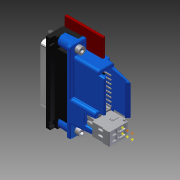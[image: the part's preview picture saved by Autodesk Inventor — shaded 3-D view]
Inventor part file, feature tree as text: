
AUTODESK INVENTOR PART (.ipt)
format: ipt  version: 2011 (Build 150239000, 239)  size: 2,223,616 bytes
history: native  units: in
note: dims shown in document units (in); Inventor stores cm internally (conversion verified against a paired STEP export)
features: other x22, plane x4, pattern_linear x1
ambient origin geometry x8: Origin, YZ Plane, XZ Plane, XY Plane, X Axis, Y Axis, Z Axis, Center Point
bodies: Solid1 (feature_tree)
feature tree (27):
  other  "Relay Bumper Assembly.iam"
  other  "Relay Bumper Board Assembly.iam:1::Relay Board Rev2.ipt:1"
  other  "Relay Bumper Board Assembly.iam:1::R2512_C_0_0236_R.ipt:1"
  other  "Relay Bumper Board Assembly.iam:1::SO-8_M_FET_0_0689_Q.ipt:1"
  other  "Relay Bumper Board Assembly.iam:1::LED1208RA_LiteOn_0_0394_D.ipt:1"
  other  "Relay Bumper Board Assembly.iam:1::Right Angle Connector.ipt:1"
  other  "Relay Bumper Board Assembly.iam:1::734-162:1"
  other  "Relay Bumper Board Assembly.iam:1::C-5747846-02-3.ipt:1"
  other  "Relay Muzzle Rev2.ipt:1"
  other  "4-40 SHCS.ipt:1"
  other  "4-40 SHCS.ipt:2"
  other  "Relay Bumper Assembly.iam_Bodies"
  plane  "Work Plane1"
  plane  "Work Plane2"
  other  "Work Point1"
  other  "Work Point2"
  other  "Work Point3"
  pattern_linear  "Rectangular Pattern1"  Spacing1=0.3937in  [1 undecoded]
  other  "Work Axis1"
  other  "Work Axis2"
  plane  "Work Plane3"
  other  "Work Axis3"
  plane  "Work Plane4"
  other  "Work Axis4"
  other  "Work Point4"
  other  "Work Point5"
  other  "Work Point6"
note: 1 required parameter value undecoded (feature->parameter linkage not recoverable at this tier; creation-order binding heuristic only, values carry confidence <= 0.55)
